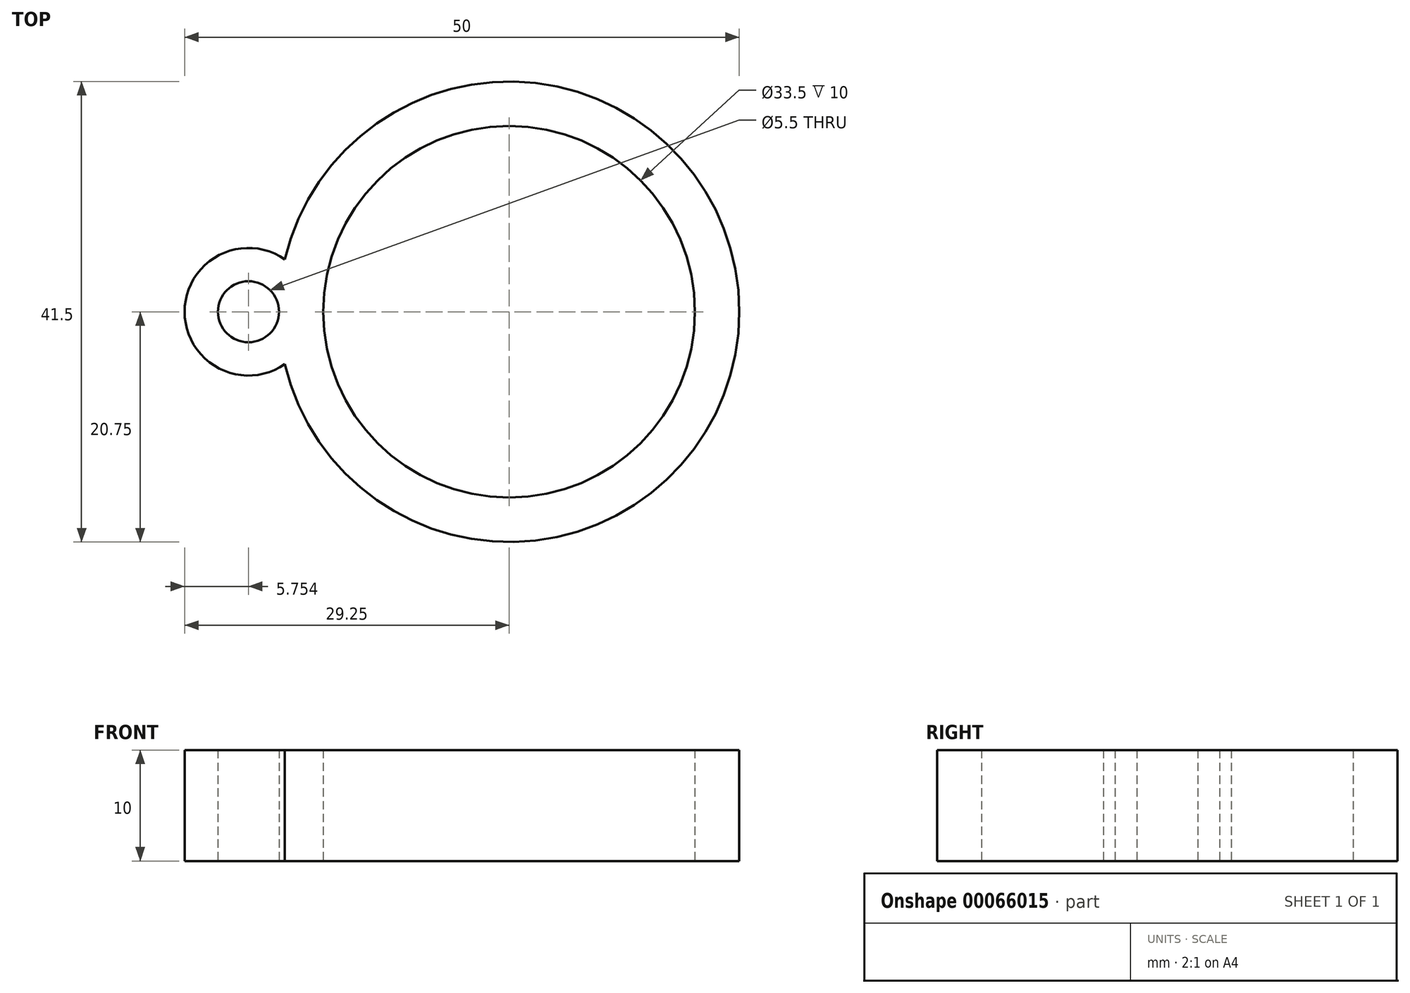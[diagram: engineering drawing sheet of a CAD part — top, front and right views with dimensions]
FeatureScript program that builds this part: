
annotation { "Feature Type Name" : "Feature", "Feature Type Description" : "" }
export const myFeature = defineFeature(function(context is Context, id is Id, definition is map)
    precondition{}
    {
        {
            var Q0;
            Q0=qCreatedBy(makeId("Top.planeOp"),FACE);
            var sketch = newSketch(context, id + "F0", { "sketchPlane" : qUnion([Q0])});
            skCircle(sketch, "E0", {"center": v(0, 0) * mm, "radius": 16.75 * mm});
            skArc(sketch, "E1", {"start": v(-20.75, 0.14) * mm, "mid": v(-20.75, 0) * mm, "end": v(-20.75, -0.14) * mm});
            skCircle(sketch, "E2", {"center": v(-23.5, 0) * mm, "radius": 2.75 * mm});
            skArc(sketch, "E3", {"start": v(-20.2, 4.72) * mm, "mid": v(-29.25, 0) * mm, "end": v(-20.2, -4.72) * mm});
            skArc(sketch, "E4.trimOffspring", {"start": v(-20.2, -4.72) * mm, "mid": v(20.75, 0) * mm, "end": v(-20.2, 4.72) * mm});
            skSolve(sketch);
        }
        {
            var Q0;
            Q0=makeQuery(id+"F0.imprint","IMPRINT",FACE,{"disambiguationData":[TD([[makeQuery(id+"F0.imprint","IMPRINT",EDGE,{"derivedFrom":sQuery(id+"F0.wireOp",EDGE,"E0")}),-1.0]])]});
            extrude(context, id + "F1", {"entities" : qUnion([Q0]), "depth" : 10 * mm});
        }
    });
